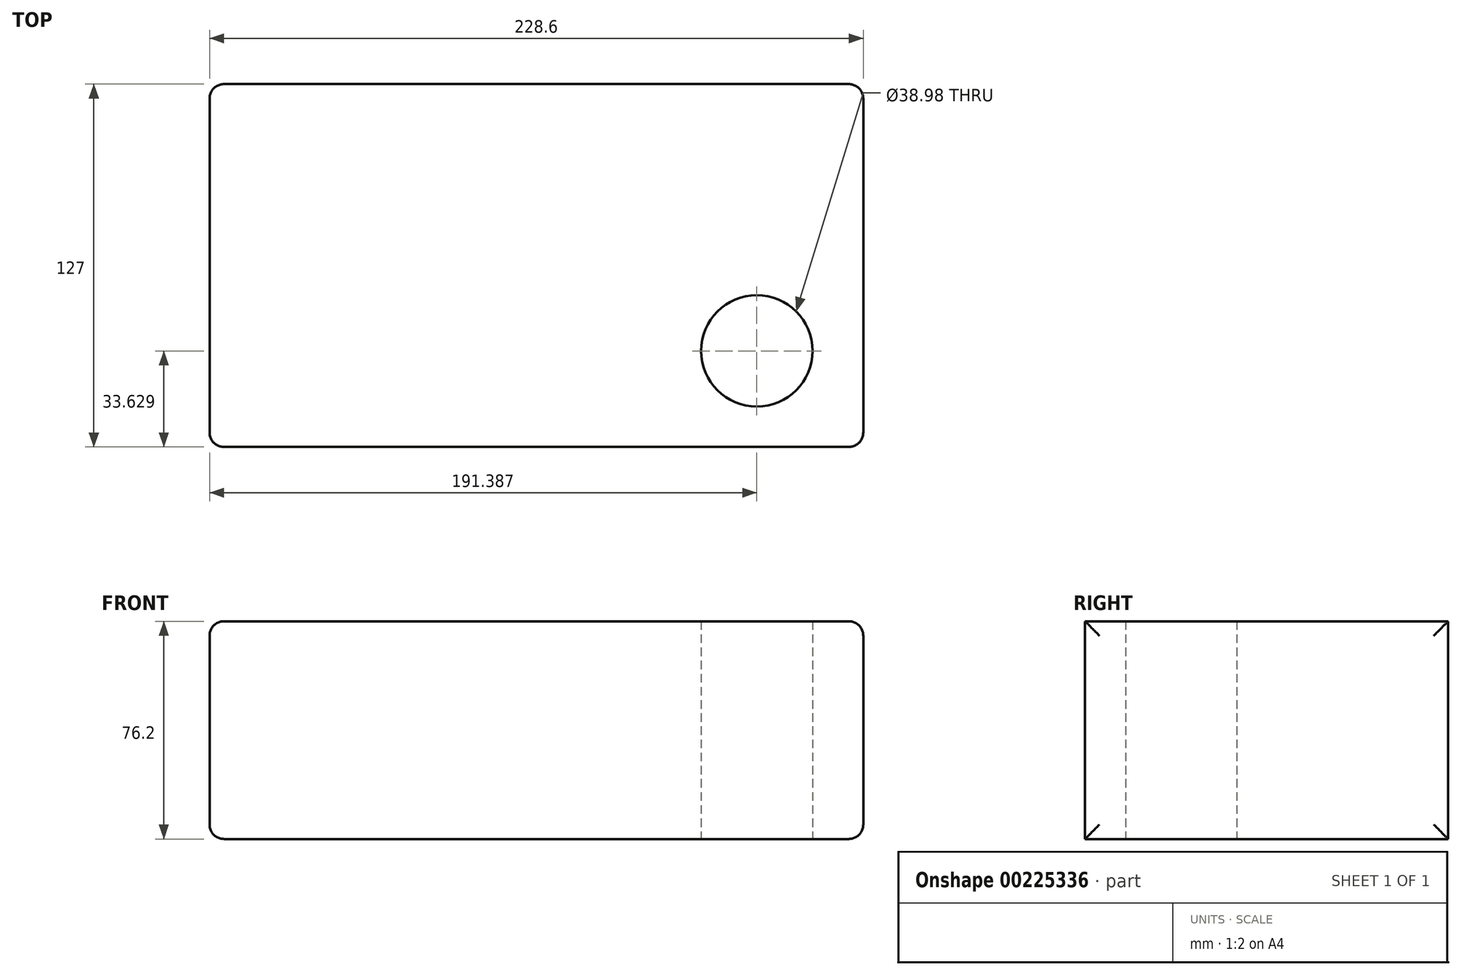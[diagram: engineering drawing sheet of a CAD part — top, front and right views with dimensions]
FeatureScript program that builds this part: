
annotation { "Feature Type Name" : "Feature", "Feature Type Description" : "" }
export const myFeature = defineFeature(function(context is Context, id is Id, definition is map)
    precondition{}
    {
        {
            var Q0;
            Q0=qCreatedBy(makeId("Top.planeOp"),FACE);
            var sketch = newSketch(context, id + "F0", { "sketchPlane" : qUnion([Q0])});
            skLineSegment(sketch, "E0.bottom", {"start": v(114.3, -63.5) * mm, "end": v(-114.3, -63.5) * mm});
            skLineSegment(sketch, "E0.top", {"start": v(114.3, 63.5) * mm, "end": v(-114.3, 63.5) * mm});
            skLineSegment(sketch, "E0.left", {"start": v(114.3, -63.5) * mm, "end": v(114.3, 63.5) * mm});
            skLineSegment(sketch, "E0.right", {"start": v(-114.3, -63.5) * mm, "end": v(-114.3, 63.5) * mm});
            skPoint(sketch, "E0.middle", {"position": v(0, 0) * mm});
            skCircle(sketch, "E1", {"center": v(77.09, -29.87) * mm, "radius": 19.5 * mm});
            skSolve(sketch);
        }
        {
            var Q0;
            Q0=makeQuery(id+"F0.imprint","IMPRINT",FACE,{"disambiguationData":[TD([[makeQuery(id+"F0.imprint","IMPRINT",EDGE,{"derivedFrom":sQuery(id+"F0.wireOp",EDGE,"E0.bottom")}),-1.0]])]});
            extrude(context, id + "F1", {"entities" : qUnion([Q0]), "depth" : 76.2 * mm});
        }
        {
            var Q0;
            Q0=makeQuery(id+"F1.opExtrude","SWEPT_FACE",FACE,{"disambiguationData":[OSD([sQuery(id+"F0.wireOp",EDGE,"E0.right")])]});
            fillet(context, id + "F2", {"entities" : qUnion([Q0]), "radius" : 5.08 * mm, "tangentPropagation" : true, "allowEdgeOverflow" : false});
        }
        {
            var Q0;
            Q0=makeQuery(id+"F1.opExtrude","SWEPT_FACE",FACE,{"disambiguationData":[OSD([sQuery(id+"F0.wireOp",EDGE,"E0.left")])]});
            fillet(context, id + "F3", {"entities" : qUnion([Q0]), "radius" : 5.08 * mm, "tangentPropagation" : true, "allowEdgeOverflow" : false});
        }
        {
            var Q0;
            Q0=makeQuery(id+"F0.imprint","IMPRINT",FACE,{"disambiguationData":[TD([[makeQuery(id+"F0.imprint","IMPRINT",EDGE,{"derivedFrom":sQuery(id+"F0.wireOp",EDGE,"E1")}),1.0]])]});
            extrude(context, id + "F4", {"entities" : qUnion([Q0]), "operationType" : NewBodyOperationType.REMOVE, "depth" : 25.4 * mm});
        }
    });
